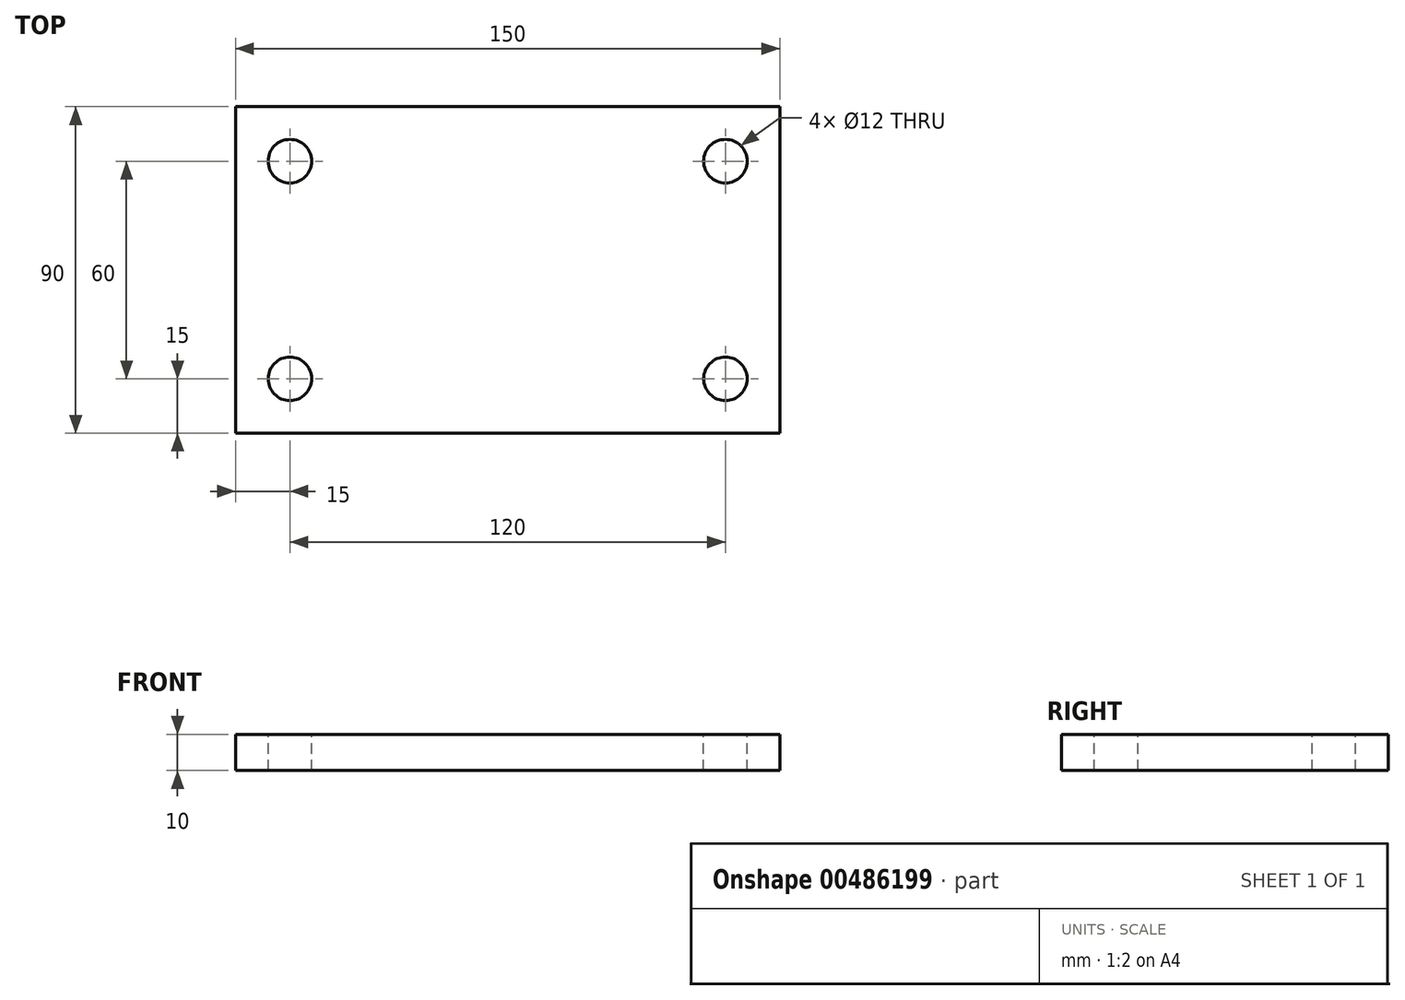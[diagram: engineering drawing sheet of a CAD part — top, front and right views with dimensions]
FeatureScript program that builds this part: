
annotation { "Feature Type Name" : "Feature", "Feature Type Description" : "" }
export const myFeature = defineFeature(function(context is Context, id is Id, definition is map)
    precondition{}
    {
        {
            var Q0;
            Q0=qCreatedBy(makeId("Top.planeOp"),FACE);
            var sketch = newSketch(context, id + "F0", { "sketchPlane" : qUnion([Q0])});
            skLineSegment(sketch, "E0.bottom", {"start": v(-75, -45) * mm, "end": v(75, -45) * mm});
            skLineSegment(sketch, "E0.top", {"start": v(-75, 45) * mm, "end": v(75, 45) * mm});
            skLineSegment(sketch, "E0.left", {"start": v(-75, -45) * mm, "end": v(-75, 45) * mm});
            skLineSegment(sketch, "E0.right", {"start": v(75, -45) * mm, "end": v(75, 45) * mm});
            skSolve(sketch);
        }
        {
            var Q0;
            Q0 = qSketchRegion(id + "F0", true);
            extrude(context, id + "F1", {"entities" : qUnion([Q0]), "endBound" : BoundingType.SYMMETRIC, "depth" : 10 * mm});
        }
        {
            var Q0;
            Q0=makeQuery(id+"F1.opExtrude","CAP_FACE",FACE,{"disambiguationData":[OSD([sQuery(id+"F0.wireOp",EDGE,"E0.bottom"),sQuery(id+"F0.wireOp",EDGE,"E0.top"),sQuery(id+"F0.wireOp",EDGE,"E0.left"),sQuery(id+"F0.wireOp",EDGE,"E0.right")])],"isStart":false});
            var sketch = newSketch(context, id + "F2", { "sketchPlane" : qUnion([Q0])});
            skPoint(sketch, "E1", {"position": v(-60, 30) * mm});
            skPoint(sketch, "E2", {"position": v(-60, -30) * mm});
            skPoint(sketch, "E3", {"position": v(60, 30) * mm});
            skPoint(sketch, "E4", {"position": v(60, -30) * mm});
            skSolve(sketch);
        }
        {
            var Q0;
            Q0=sQuery(id+"F2.wireOp",VERTEX,"E1");
            var Q1;
            Q1=sQuery(id+"F2.wireOp",VERTEX,"E2");
            var Q2;
            Q2=sQuery(id+"F2.wireOp",VERTEX,"E4");
            var Q3;
            Q3=sQuery(id+"F2.wireOp",VERTEX,"E3");
            var Q4;
            Q4=makeQuery(id+"F1.opExtrude","SWEPT_BODY",BODY,{"disambiguationData":[OSD([sQuery(id+"F0.wireOp",EDGE,"E0.bottom"),sQuery(id+"F0.wireOp",EDGE,"E0.top"),sQuery(id+"F0.wireOp",EDGE,"E0.left"),sQuery(id+"F0.wireOp",EDGE,"E0.right")])]});
            hole(context, id + "F3", {"style" : HoleStyle.SIMPLE, "endStyle" : HoleEndStyle.THROUGH, "holeDiameter" : 12 * mm, "isTappedThrough" : true, "tappedDepth" : 12 * mm, "tapClearance" : 3, "locations" : qUnion([Q0, Q1, Q2, Q3]), "scope" : qUnion([Q4])});
        }
    });
